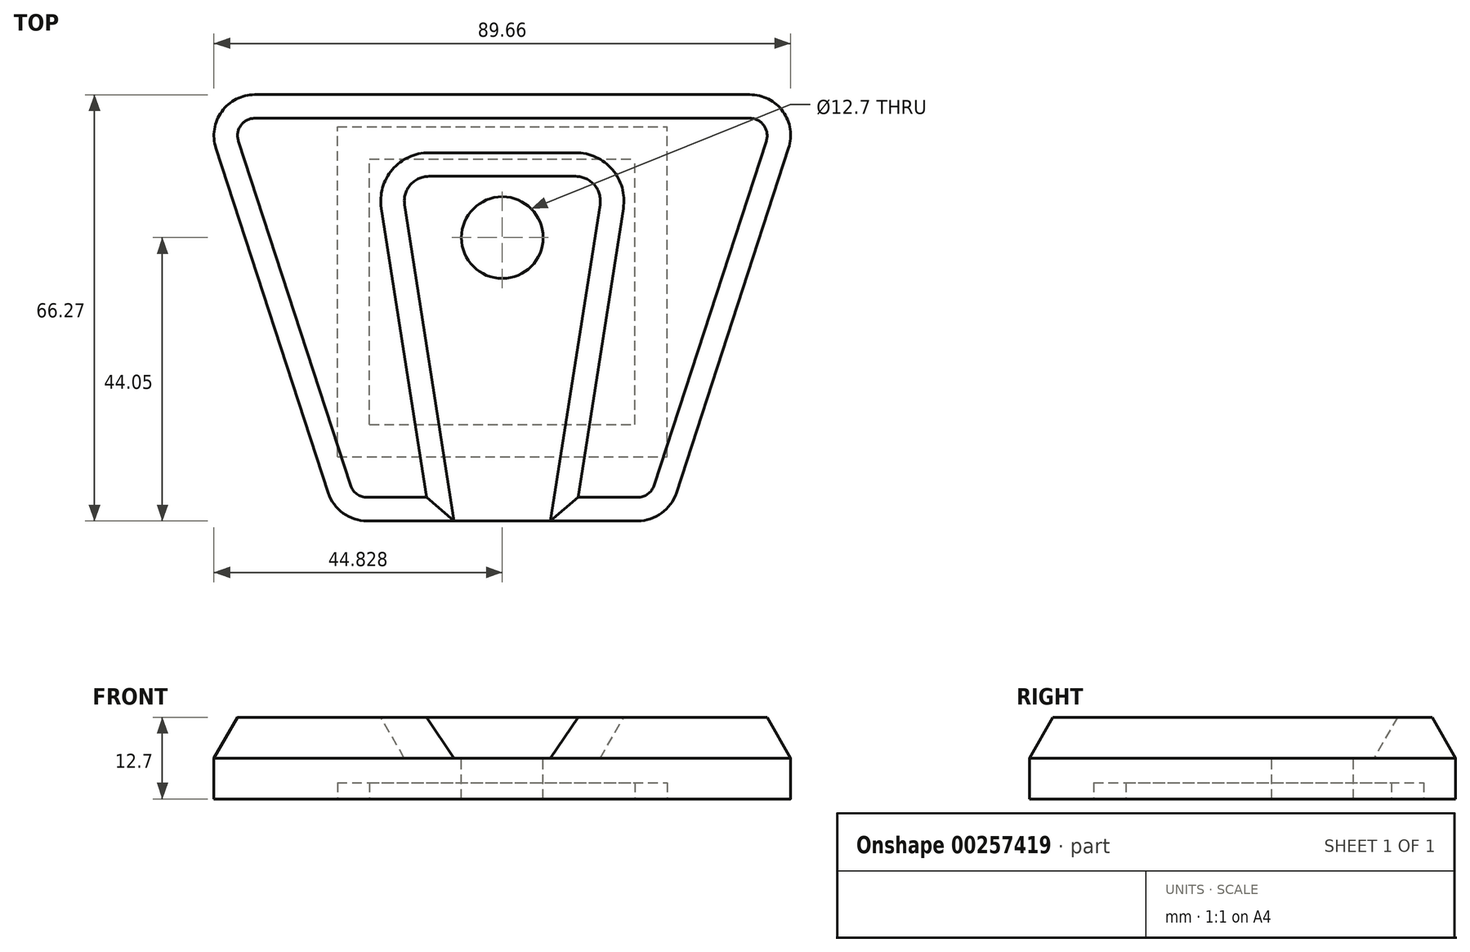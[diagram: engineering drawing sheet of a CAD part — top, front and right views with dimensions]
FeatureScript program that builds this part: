
annotation { "Feature Type Name" : "Feature", "Feature Type Description" : "" }
export const myFeature = defineFeature(function(context is Context, id is Id, definition is map)
    precondition{}
    {
        {
            var Q0;
            Q0=qCreatedBy(makeId("Top.planeOp"),FACE);
            var sketch = newSketch(context, id + "F0", { "sketchPlane" : qUnion([Q0])});
            skLineSegment(sketch, "E0.bottom", {"start": v(0, 0) * mm, "end": v(51.27, 0) * mm, "construction": true});
            skLineSegment(sketch, "E0.top", {"start": v(0, 51.27) * mm, "end": v(51.27, 51.27) * mm, "construction": true});
            skLineSegment(sketch, "E0.left", {"start": v(0, 0) * mm, "end": v(0, 51.27) * mm, "construction": true});
            skLineSegment(sketch, "E0.right", {"start": v(51.27, 0) * mm, "end": v(51.27, 51.27) * mm, "construction": true});
            skLineSegment(sketch, "E1", {"start": v(25.64, 51.27) * mm, "end": v(25.64, 0) * mm, "construction": true});
            skLineSegment(sketch, "E2", {"start": v(25.64, 56.27) * mm, "end": v(-12.84, 56.27) * mm});
            skLineSegment(sketch, "E3", {"start": v(-18.88, 47.96) * mm, "end": v(-1.43, -5.62) * mm});
            skLineSegment(sketch, "E4", {"start": v(4.6, -10) * mm, "end": v(25.64, -10) * mm});
            skPoint(sketch, "E5.visualSharp", {"position": v(-21.6, 56.27) * mm});
            skArc(sketch, "E5.filletArc", {"start": v(-12.84, 56.27) * mm, "mid": v(-17.98, 53.66) * mm, "end": v(-18.88, 47.96) * mm});
            skPoint(sketch, "E6.visualSharp", {"position": v(0, -10) * mm});
            skArc(sketch, "E6.filletArc", {"start": v(-1.43, -5.62) * mm, "mid": v(0.88, -8.79) * mm, "end": v(4.6, -10) * mm});
            skLineSegment(sketch, "E7.MirrorCS", {"start": v(25.64, 56.27) * mm, "end": v(64.12, 56.27) * mm});
            skArc(sketch, "E8.MirrorCS", {"start": v(64.12, 56.27) * mm, "mid": v(69.26, 53.66) * mm, "end": v(70.16, 47.96) * mm});
            skLineSegment(sketch, "E9.MirrorCS", {"start": v(70.16, 47.96) * mm, "end": v(52.7, -5.62) * mm});
            skArc(sketch, "E10.MirrorCS", {"start": v(52.7, -5.62) * mm, "mid": v(50.4, -8.79) * mm, "end": v(46.67, -10) * mm});
            skLineSegment(sketch, "E11.MirrorCS", {"start": v(46.67, -10) * mm, "end": v(25.64, -10) * mm});
            skLineSegment(sketch, "E12", {"start": v(18.14, -10) * mm, "end": v(10.45, 39.18) * mm});
            skLineSegment(sketch, "E13", {"start": v(14.21, 43.57) * mm, "end": v(37.06, 43.57) * mm});
            skLineSegment(sketch, "E14", {"start": v(40.82, 39.18) * mm, "end": v(33.14, -10) * mm});
            skPoint(sketch, "E15.visualSharp", {"position": v(9.76, 43.57) * mm});
            skArc(sketch, "E15.filletArc", {"start": v(14.21, 43.57) * mm, "mid": v(11.32, 42.24) * mm, "end": v(10.45, 39.18) * mm});
            skPoint(sketch, "E16.visualSharp", {"position": v(41.51, 43.57) * mm});
            skArc(sketch, "E16.filletArc", {"start": v(40.82, 39.18) * mm, "mid": v(39.96, 42.24) * mm, "end": v(37.06, 43.57) * mm});
            skSolve(sketch);
        }
        {
            var Q0;
            Q0 = qSketchRegion(id + "F0", true);
            extrude(context, id + "F1", {"entities" : qUnion([Q0]), "oppositeDirection" : true, "depth" : 6.35 * mm});
        }
        {
            var Q0;
            Q0=makeQuery(id+"F0.imprint","IMPRINT",FACE,{"disambiguationData":[TD([[makeQuery(id+"F0.imprint","IMPRINT",EDGE,{"derivedFrom":sQuery(id+"F0.wireOp",EDGE,"E2")}),1.0]])]});
            extrude(context, id + "F2", {"entities" : qUnion([Q0]), "operationType" : NewBodyOperationType.ADD, "depth" : 6.35 * mm, "hasDraft" : true, "draftAngle" : 30 * degree, "draftPullDirection" : true});
        }
        {
            var Q0;
            {var subQ0=sQuery(id+"F0.wireOp",EDGE,"E12");Q0=makeQuery(id+"F0.imprint","IMPRINT",FACE,{"disambiguationData":[TD([[makeQuery(id+"F0.imprint","IMPRINT",EDGE,{"derivedFrom":subQ0}),-1.0]])]});}
            var sketch = newSketch(context, id + "F3", { "sketchPlane" : qUnion([Q0])});
            skCircle(sketch, "E17", {"center": v(25.64, 34.05) * mm, "radius": 6.35 * mm});
            skSolve(sketch);
        }
        {
            var Q0;
            Q0 = qSketchRegion(id + "F3", true);
            extrude(context, id + "F4", {"entities" : qUnion([Q0]), "operationType" : NewBodyOperationType.REMOVE, "oppositeDirection" : true, "depth" : 25.4 * mm});
        }
        {
            var Q0;
            Q0=makeQuery(id+"F1.opExtrude","CAP_FACE",FACE,{"disambiguationData":[OSD([sQuery(id+"F0.wireOp",EDGE,"E2"),sQuery(id+"F0.wireOp",EDGE,"E3"),sQuery(id+"F0.wireOp",EDGE,"E4"),sQuery(id+"F0.wireOp",EDGE,"E5.filletArc"),sQuery(id+"F0.wireOp",EDGE,"E6.filletArc"),sQuery(id+"F0.wireOp",EDGE,"E7.MirrorCS"),sQuery(id+"F0.wireOp",EDGE,"E8.MirrorCS"),sQuery(id+"F0.wireOp",EDGE,"E9.MirrorCS"),sQuery(id+"F0.wireOp",EDGE,"E10.MirrorCS"),sQuery(id+"F0.wireOp",EDGE,"E11.MirrorCS")])],"isStart":false});
            var sketch = newSketch(context, id + "F5", { "sketchPlane" : qUnion([Q0])});
            skLineSegment(sketch, "E18.bottom", {"start": v(0, 0) * mm, "end": v(51.28, 0) * mm});
            skLineSegment(sketch, "E18.top", {"start": v(0, -51.28) * mm, "end": v(51.28, -51.28) * mm});
            skLineSegment(sketch, "E18.left", {"start": v(0, 0) * mm, "end": v(0, -51.28) * mm});
            skLineSegment(sketch, "E18.right", {"start": v(51.28, 0) * mm, "end": v(51.28, -51.28) * mm});
            skLineSegment(sketch, "E19.bottom", {"start": v(5, -5) * mm, "end": v(46.28, -5) * mm});
            skLineSegment(sketch, "E19.top", {"start": v(5, -46.28) * mm, "end": v(46.28, -46.28) * mm});
            skLineSegment(sketch, "E19.left", {"start": v(5, -5) * mm, "end": v(5, -46.28) * mm});
            skLineSegment(sketch, "E19.right", {"start": v(46.28, -5) * mm, "end": v(46.28, -46.28) * mm});
            skPoint(sketch, "E19.middle", {"position": v(25.64, -25.64) * mm});
            skPoint(sketch, "E19.middle.positionSnap0", {"position": v(25.64, 0) * mm});
            skPoint(sketch, "E19.middle.positionSnap1", {"position": v(0, -25.64) * mm});
            skPoint(sketch, "E19.centerSnap0", {"position": v(25.64, 0) * mm});
            skPoint(sketch, "E19.centerSnap1", {"position": v(0, -25.64) * mm});
            skSolve(sketch);
        }
        {
            var Q0;
            Q0 = qSketchRegion(id + "F5", true);
            extrude(context, id + "F6", {"entities" : qUnion([Q0]), "operationType" : NewBodyOperationType.REMOVE, "oppositeDirection" : true, "depth" : 2.54 * mm});
        }
    });
